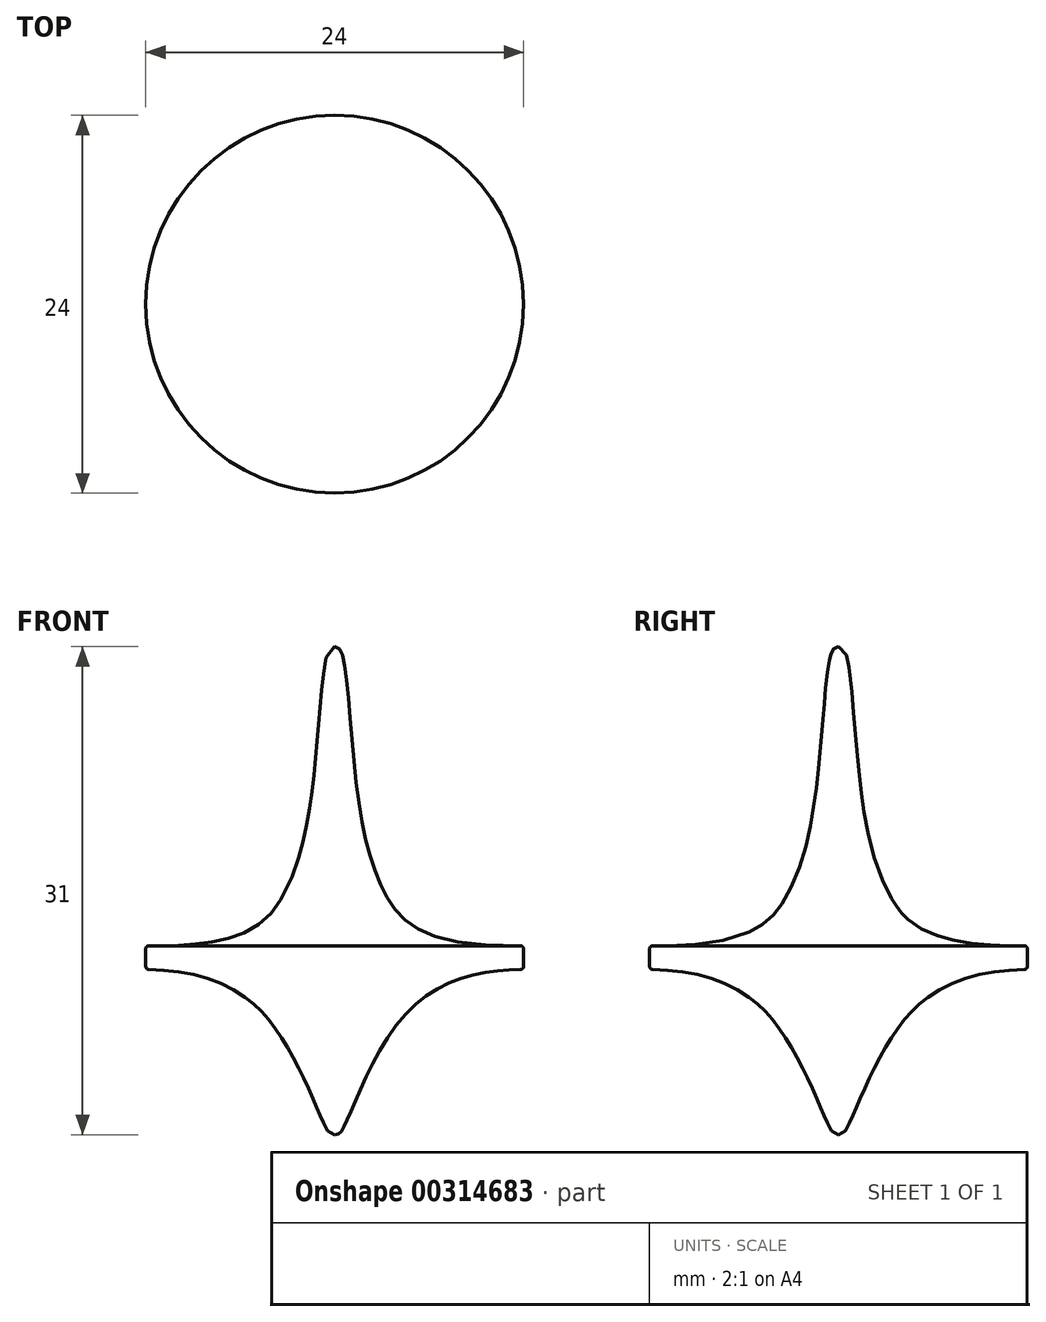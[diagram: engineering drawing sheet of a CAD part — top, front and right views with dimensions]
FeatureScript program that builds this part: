
annotation { "Feature Type Name" : "Feature", "Feature Type Description" : "" }
export const myFeature = defineFeature(function(context is Context, id is Id, definition is map)
    precondition{}
    {
        {
            var Q0;
            Q0=qCreatedBy(makeId("Front.planeOp"),FACE);
            var sketch = newSketch(context, id + "F0", { "sketchPlane" : qUnion([Q0])});
            skLineSegment(sketch, "E0", {"start": v(0, 0) * mm, "end": v(0, 31) * mm});
            skFitSpline(sketch, "E1", {"points": [v(0, 0) * mm, v(0.69, 0.7) * mm, v(4.95, 8.12) * mm, v(12, 10.5) * mm], "startDerivative": vector(6.42, 0) * mm, "endDerivative": vector(16.12, 0.23) * mm});
            skLineSegment(sketch, "E2", {"start": v(12, 10.5) * mm, "end": v(12, 12) * mm});
            skFitSpline(sketch, "E3", {"points": [v(12, 12) * mm, v(3.17, 15.36) * mm, v(1.4, 22.03) * mm, v(0.53, 30.34) * mm, v(0, 31) * mm], "startDerivative": vector(-57.72, -1.04) * mm, "endDerivative": vector(-9.36, 0.46) * mm});
            skSolve(sketch);
        }
        {
            var Q0;
            Q0=makeQuery(id+"F0.imprint","IMPRINT",FACE,{"disambiguationData":[TD([[makeQuery(id+"F0.imprint","IMPRINT",EDGE,{"derivedFrom":sQuery(id+"F0.wireOp",EDGE,"E0")}),-1.0]])]});
            var Q1;
            Q1=sQuery(id+"F0.wireOp",EDGE,"E0");
            revolve(context, id + "F1", {"surfaceOperationType" : NewSurfaceOperationType.NEW, "entities" : qUnion([Q0]), "axis" : qUnion([Q1]), "revolveType" : RevolveType.FULL});
        }
        {
            var Q0;
            Q0=makeQuery(id+"F1.opRevolve","SWEPT_EDGE",EDGE,{"disambiguationData":[OSD([sQuery(id+"F0.wireOp",EDGE,"E1"),sQuery(id+"F0.wireOp",EDGE,"E2")])]});
            var Q1;
            Q1=makeQuery(id+"F1.opRevolve","SWEPT_EDGE",EDGE,{"disambiguationData":[OSD([sQuery(id+"F0.wireOp",EDGE,"E2"),sQuery(id+"F0.wireOp",EDGE,"E3")])]});
            fillet(context, id + "F2", {"entities" : qUnion([Q0, Q1]), "radius" : 0.2 * mm, "tangentPropagation" : true, "allowEdgeOverflow" : false});
        }
    });
